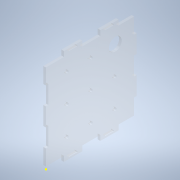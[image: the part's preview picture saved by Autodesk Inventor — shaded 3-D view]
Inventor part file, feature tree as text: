
AUTODESK INVENTOR PART (.ipt)
format: ipt  version: 2021 (Build 250183000, 183)  size: 193,536 bytes
history: native  units: mm
features: sketch x11, hole x9, extrude x1
ambient origin geometry x8: Origin, YZ Plane, XZ Plane, XY Plane, X Axis, Y Axis, Z Axis, Center Point
bodies: Solid1 (feature_tree)
feature tree (21):
  extrude  "Extrusion1"  Depth=3.0mm
  hole  "Hole2"  [1 undecoded]
  hole  "Hole3"  [1 undecoded]
  hole  "Hole4"  [1 undecoded]
  hole  "Hole5"  [1 undecoded]
  hole  "Hole6"  [1 undecoded]
  hole  "Hole7"  [1 undecoded]
  hole  "Hole8"  [1 undecoded]
  hole  "Hole9"  [1 undecoded]
  sketch  "Sketch11"  dims[d87=15.0mm d88=6.0mm d89=4.0mm d90=2.0mm d91=90.0deg d92=8.0mm d93=20.594885mm d94=1.0mm]
  hole  "Hole10"  [1 undecoded]
  sketch  "Sketch1"  dims[d4=3.0mm d5=0.0mm d22=3.0mm]
  sketch  "Sketch3"  dims[d23=3.0mm d24=6.0mm d25=4.0mm d26=2.0mm d27=90.0deg d28=8.0mm d29=20.594885mm d30=3.0mm]
  sketch  "Sketch4"  dims[d31=3.0mm d32=6.0mm d33=4.0mm d34=2.0mm d35=90.0deg d36=8.0mm d37=20.594885mm d38=3.0mm]
  sketch  "Sketch5"  dims[d39=3.0mm d40=6.0mm d41=4.0mm d42=2.0mm d43=90.0deg d44=8.0mm d45=20.594885mm d46=3.0mm]
  sketch  "Sketch6"  dims[d47=3.0mm d48=6.0mm d49=4.0mm d50=2.0mm d51=90.0deg d52=8.0mm d53=20.594885mm d54=3.0mm]
  sketch  "Sketch7"  dims[d55=3.0mm d56=6.0mm d57=4.0mm d58=2.0mm d59=90.0deg d60=8.0mm d61=20.594885mm d62=3.0mm]
  sketch  "Sketch8"  dims[d63=3.0mm d64=6.0mm d65=4.0mm d66=2.0mm d67=90.0deg d68=8.0mm d69=20.594885mm d70=3.0mm]
  sketch  "Sketch9"  dims[d71=3.0mm d72=6.0mm d73=4.0mm d74=2.0mm d75=90.0deg d76=8.0mm d77=20.594885mm d78=3.0mm]
  sketch  "Sketch10"  dims[d79=3.0mm d80=6.0mm d81=4.0mm d82=2.0mm d83=90.0deg d84=8.0mm d85=20.594885mm d86=3.0mm]
  sketch  "Sketch12"  dims[d95=10.0mm d96=10.0mm d97=1.0mm d98=10.0mm d99=1.0mm d100=10.0mm]
note: 9 required parameter values undecoded (feature->parameter linkage not recoverable at this tier; creation-order binding heuristic only, values carry confidence <= 0.55)
